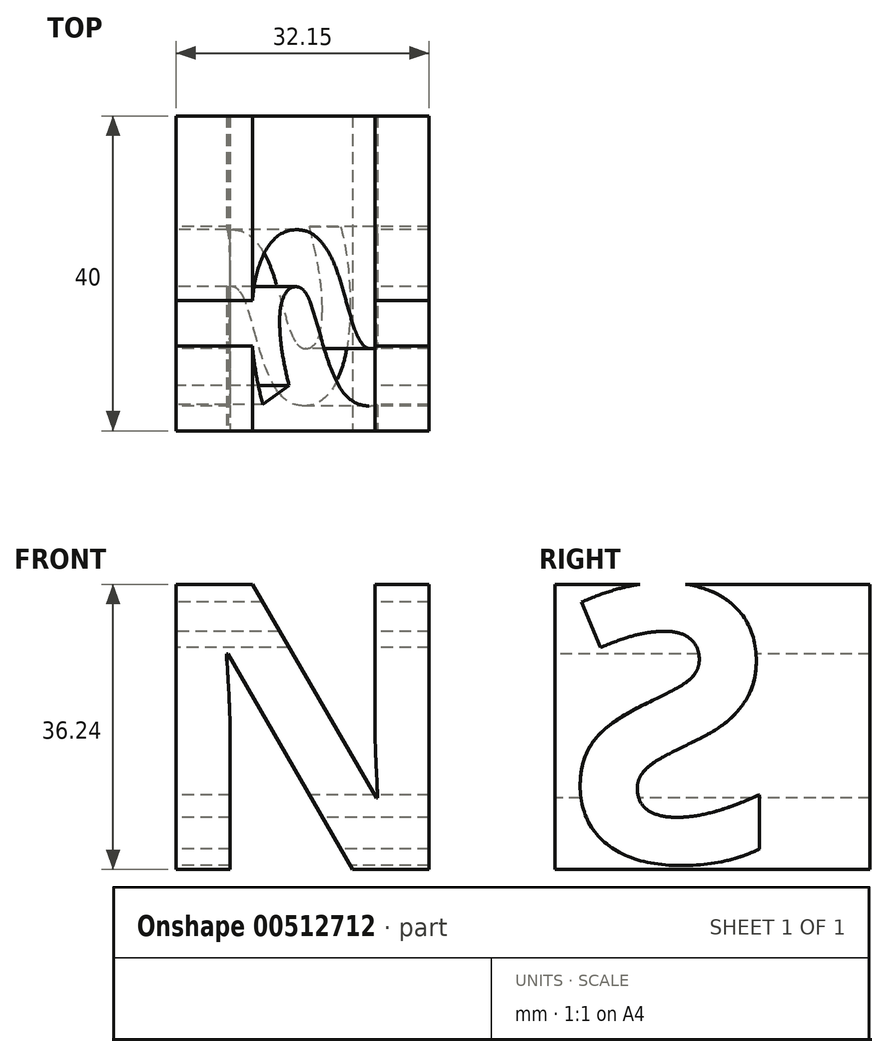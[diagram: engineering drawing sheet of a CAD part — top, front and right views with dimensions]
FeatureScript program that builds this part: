
annotation { "Feature Type Name" : "Feature", "Feature Type Description" : "" }
export const myFeature = defineFeature(function(context is Context, id is Id, definition is map)
    precondition{}
    {
        {
            var Q0;
            Q0=qCreatedBy(makeId("Front.planeOp"),FACE);
            var sketch = newSketch(context, id + "F0", { "sketchPlane" : qUnion([Q0])});
            skLineSegment(sketch, "E0.bottom", {"start": v(-20, 20) * mm, "end": v(20, 20) * mm});
            skLineSegment(sketch, "E0.top", {"start": v(-20, -20) * mm, "end": v(20, -20) * mm});
            skLineSegment(sketch, "E0.left", {"start": v(-20, 20) * mm, "end": v(-20, -20) * mm});
            skLineSegment(sketch, "E0.right", {"start": v(20, 20) * mm, "end": v(20, -20) * mm});
            skPoint(sketch, "E0.middle", {"position": v(0, 0) * mm});
            skSolve(sketch);
        }
        {
            var Q0;
            Q0=makeQuery(id+"F0.imprint","IMPRINT",FACE,{"disambiguationData":[TD([[makeQuery(id+"F0.imprint","IMPRINT",EDGE,{"derivedFrom":sQuery(id+"F0.wireOp",EDGE,"E0.bottom")}),-1.0]])]});
            extrude(context, id + "F1", {"entities" : qUnion([Q0]), "endBound" : BoundingType.SYMMETRIC, "depth" : 40 * mm});
        }
        {
            var Q0;
            Q0=makeQuery(id+"F1.opExtrude","CAP_FACE",FACE,{"disambiguationData":[OSD([sQuery(id+"F0.wireOp",EDGE,"E0.bottom"),sQuery(id+"F0.wireOp",EDGE,"E0.top"),sQuery(id+"F0.wireOp",EDGE,"E0.left"),sQuery(id+"F0.wireOp",EDGE,"E0.right")])],"isStart":false});
            var sketch = newSketch(context, id + "F2", { "sketchPlane" : qUnion([Q0])});
            skText(sketch, "E1", { "text": "N", "fontName": "OpenSans-Bold.ttf"});
            const initialGuessF2  = {"E1": [-0.02, -0.01655, 1, 0, 0.03655]};
            skSetInitialGuess(sketch, initialGuessF2);
            skSolve(sketch);
        }
        {
            var Q0;
            Q0=makeQuery(id+"F2.imprint","IMPRINT",FACE,{"disambiguationData":[TD([[makeQuery(id+"F2.imprint","IMPRINT",EDGE,{"derivedFrom":sQuery(id+"F2.wireOp",EDGE,"E1.sketch_text.stroke-0")}),1.0]])]});
            extrude(context, id + "F3", {"entities" : qUnion([Q0]), "operationType" : NewBodyOperationType.REMOVE, "endBound" : BoundingType.THROUGH_ALL, "oppositeDirection" : true, "depth" : 25.4 * mm});
        }
        {
            var Q0;
            Q0=makeQuery(id+"F3.boolean.opBoolean","COPY",FACE,{"derivedFrom":makeQuery(id+"F3.opExtrude","SWEPT_FACE",FACE,{"disambiguationData":[OSD([sQuery(id+"F2.wireOp",EDGE,"E1.sketch_text.stroke-6")])]})});
            var sketch = newSketch(context, id + "F4", { "sketchPlane" : qUnion([Q0])});
            skText(sketch, "E2", { "text": "S", "fontName": "OpenSans-Bold.ttf"});
            const initialGuessF4  = {"E2": [-0.0082, -0.01556, 1, 0, 0.03525]};
            skSetInitialGuess(sketch, initialGuessF4);
            skSolve(sketch);
        }
        {
            var Q0;
            Q0=makeQuery(id+"F4.imprint","IMPRINT",FACE,{"disambiguationData":[TD([[makeQuery(id+"F4.imprint","IMPRINT",EDGE,{"derivedFrom":sQuery(id+"F4.wireOp",EDGE,"E2.sketch_text.stroke-0")}),-1.0]])]});
            extrude(context, id + "F5", {"entities" : qUnion([Q0]), "operationType" : NewBodyOperationType.REMOVE, "endBound" : BoundingType.THROUGH_ALL, "oppositeDirection" : true, "depth" : 25.4 * mm});
        }
    });
